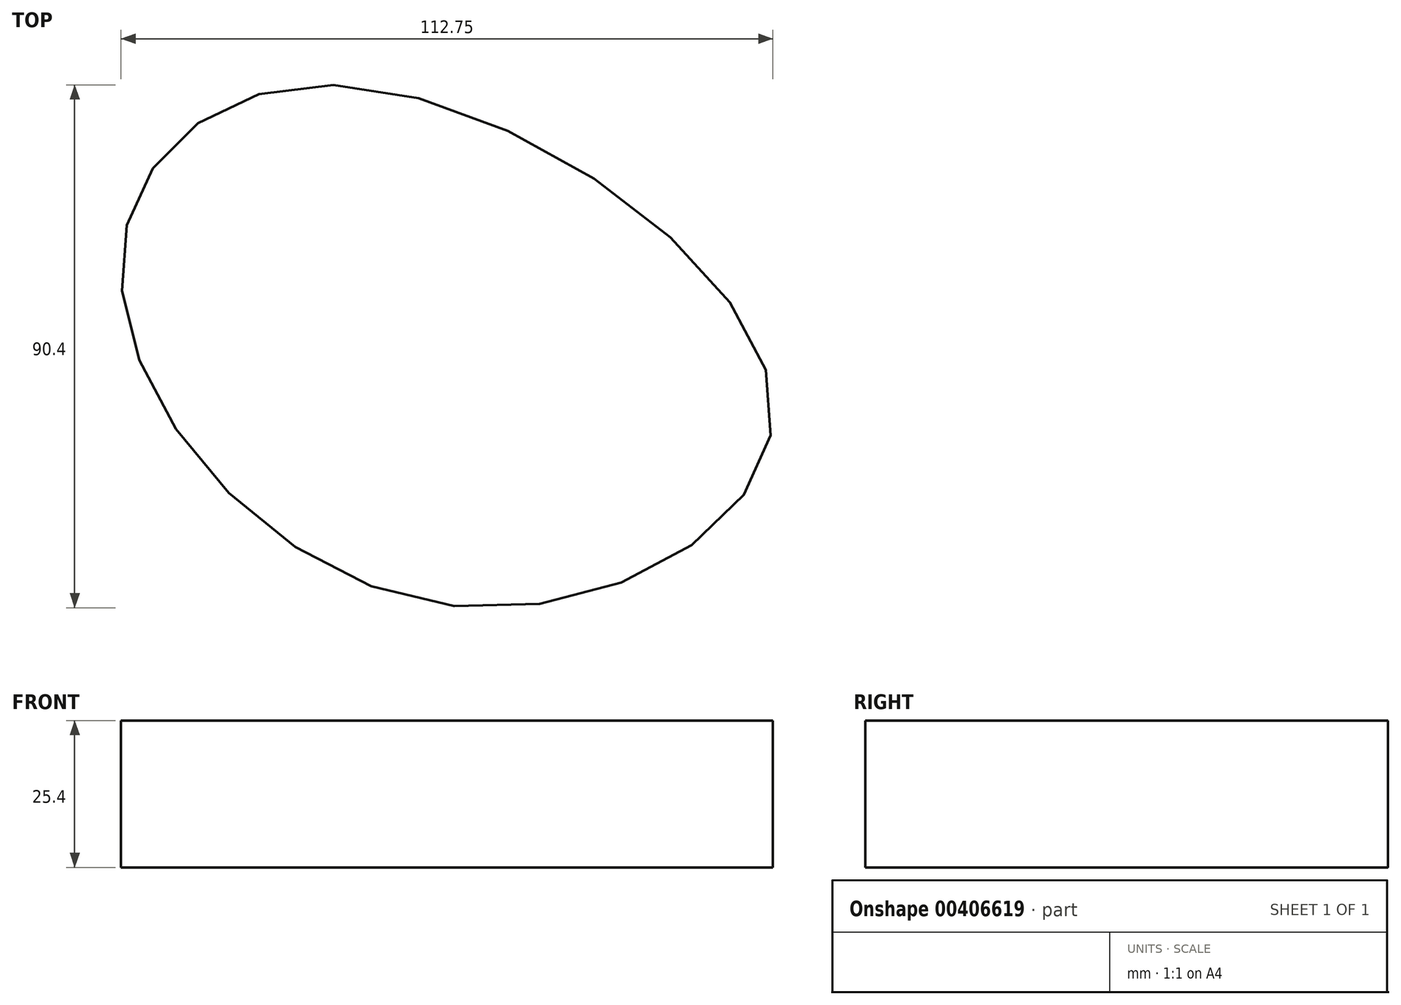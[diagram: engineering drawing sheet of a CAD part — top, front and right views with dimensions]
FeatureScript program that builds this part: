
annotation { "Feature Type Name" : "Feature", "Feature Type Description" : "" }
export const myFeature = defineFeature(function(context is Context, id is Id, definition is map)
    precondition{}
    {
        {
            var Q0;
            Q0=qCreatedBy(makeId("Top.planeOp"),FACE);
            var sketch = newSketch(context, id + "F0", { "sketchPlane" : qUnion([Q0])});
            skFitSpline(sketch, "E0", {"points": [v(-18.44, 56.3) * mm, v(-55.2, 23.31) * mm, v(0, -33.48) * mm, v(57.54, 0) * mm, v(-18.44, 56.3) * mm]});
            skSolve(sketch);
        }
        {
            var Q0;
            Q0 = qSketchRegion(id + "F0", true);
            extrude(context, id + "F1", {"entities" : qUnion([Q0]), "depth" : 25.4 * mm});
        }
    });
